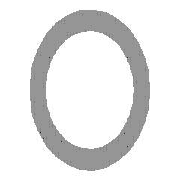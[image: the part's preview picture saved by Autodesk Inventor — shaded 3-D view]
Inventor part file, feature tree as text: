
AUTODESK INVENTOR PART (.ipt)
format: ipt  version: 2021 (Build 250183000, 183)  size: 343,040 bytes
history: native  units: mm (DEFAULTED — no unit token found)
features: other x5, plane x2, sketch x2, sweep x1
ambient origin geometry x8: Origin, YZ Plane, XZ Plane, XY Plane, X Axis, Y Axis, Z Axis, Center Point
bodies: Solid1 (feature_tree)
feature tree (10):
  parser-record x1  (decoder bookkeeping rows leaked as tree rows — omitted from the tree; the rows remain in map.json)
  other  "Driven Length"
  other  "Plano inicial"
  other  "Plano final"
  other  "Trayectoria de barrido"
  plane  "Plano de trabajo de orientación"
  sweep  "Cuerpo"
  sketch  "Sketch3"  dims[d0=21.336mm d1=3.7338mm]
  plane  "Work Plane3"
  sketch  "Sketch4"  dims[d4=-0.0mm d5=1183.592627mm d6=90.0deg d7=1183.592627mm d8=0.0mm d9=0.0mm]
